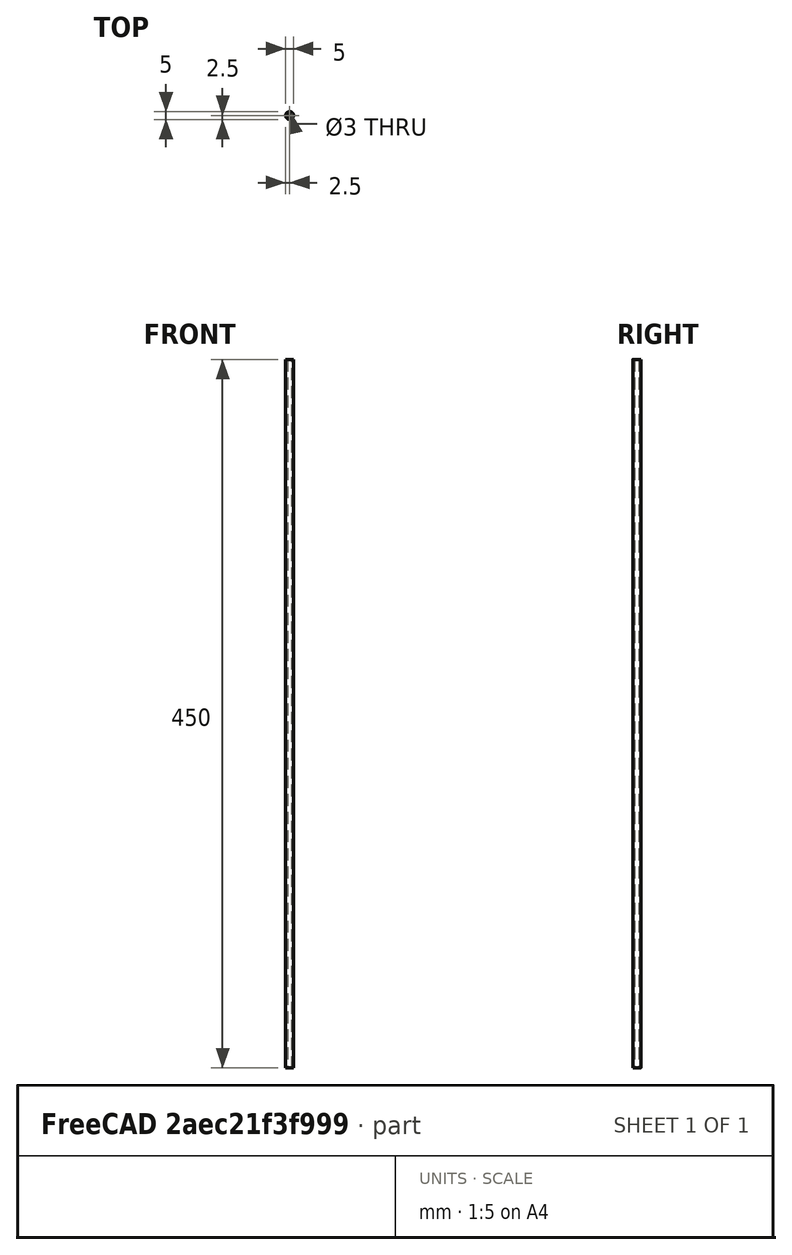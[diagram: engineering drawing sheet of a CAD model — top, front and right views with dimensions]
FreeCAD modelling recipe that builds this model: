
FCSTD DOCUMENT  (FreeCAD 1.0R39319 (Git))
Label: carbon_rod
License: All rights reserved
objects: Sketcher::SketchObject×1, PartDesign::Pad×1, PartDesign::Body×1
note: 6 computed .brp shape members not serialized (recipe doc carries the construction recipe); baked Part::Feature solids carry a one-line shape summary decoded from their .brp

FEATURE [Sketcher::SketchObject] Sketch
  ArcFitTolerance = 1e-06
  AttachmentSupport = -> [XY_Plane]
  FullyConstrained = true
  MakeInternals = false
  MapMode = 5
  sketch-geometry (2):
    g0: Circle CenterX=0 CenterY=0 CenterZ=0 NormalX=0 NormalY=0 NormalZ=1 AngleXU=0 Radius=1.5
    g1: Circle CenterX=0 CenterY=0 CenterZ=0 NormalX=0 NormalY=0 NormalZ=1 AngleXU=0 Radius=2.5
  constraints (4):
    c: Coincident(g0,g-1)
    c: Coincident(g1,g0)
    c: Diameter(g0) = 3
    c: Diameter(g1) = 5
FEATURE [PartDesign::Pad] Pad
  Direction = (0,0,1)
  Length = 450
  Length2 = 10
  Profile = -> Sketch
  ReferenceAxis = -> Sketch [N_Axis]
  Refine = true
  Suppressed = false
  Type = 0
FEATURE [PartDesign::Body] Body
  AllowCompound = false
  Group = -> [Sketch,Pad]
  Origin = -> Origin
  Tip = -> Pad
